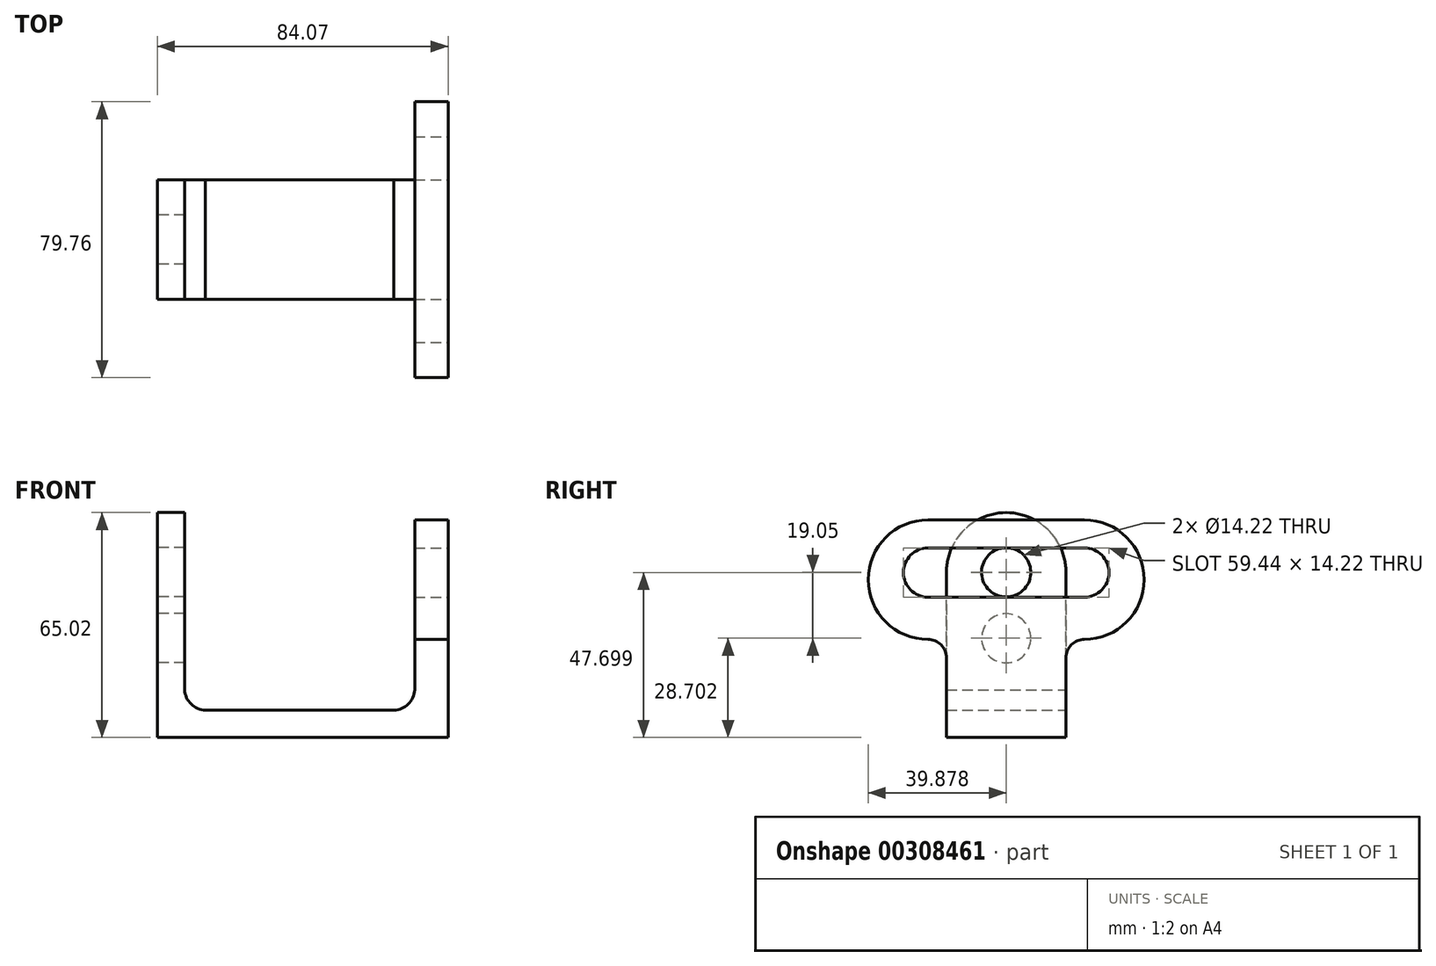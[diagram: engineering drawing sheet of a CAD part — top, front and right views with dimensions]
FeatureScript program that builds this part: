
annotation { "Feature Type Name" : "Feature", "Feature Type Description" : "" }
export const myFeature = defineFeature(function(context is Context, id is Id, definition is map)
    precondition{}
    {
        {
            var Q0;
            Q0=qCreatedBy(makeId("Front.planeOp"),FACE);
            var sketch = newSketch(context, id + "F0", { "sketchPlane" : qUnion([Q0])});
            skLineSegment(sketch, "E0", {"start": v(0, 0) * mm, "end": v(84.07, 0) * mm});
            skLineSegment(sketch, "E1", {"start": v(84.07, 0) * mm, "end": v(84.07, 46.07) * mm});
            skLineSegment(sketch, "E2", {"start": v(84.07, 46.07) * mm, "end": v(74.42, 46.07) * mm});
            skLineSegment(sketch, "E3", {"start": v(74.42, 46.07) * mm, "end": v(74.42, 13.8) * mm});
            skLineSegment(sketch, "E4", {"start": v(68.4, 7.87) * mm, "end": v(13.93, 7.87) * mm});
            skLineSegment(sketch, "E5", {"start": v(7.87, 13.8) * mm, "end": v(7.87, 47.75) * mm});
            skLineSegment(sketch, "E6", {"start": v(7.87, 47.75) * mm, "end": v(0, 47.75) * mm});
            skLineSegment(sketch, "E7", {"start": v(0, 47.75) * mm, "end": v(0, 0) * mm});
            skArc(sketch, "E8", {"start": v(7.87, 13.8) * mm, "mid": v(9.97, 9.49) * mm, "end": v(14.5, 7.87) * mm});
            skArc(sketch, "E9", {"start": v(67.77, 7.87) * mm, "mid": v(72.31, 9.48) * mm, "end": v(74.42, 13.8) * mm});
            skSolve(sketch);
        }
        {
            var Q0;
            Q0 = qSketchRegion(id + "F0", true);
            extrude(context, id + "F1", {"entities" : qUnion([Q0]), "depth" : 34.54 * mm});
        }
        {
            var Q0;
            Q0=makeQuery(id+"F1.opExtrude","SWEPT_FACE",FACE,{"disambiguationData":[OSD([sQuery(id+"F0.wireOp",EDGE,"E7")])]});
            var sketch = newSketch(context, id + "F2", { "sketchPlane" : qUnion([Q0])});
            skArc(sketch, "E10", {"start": v(34.54, 47.75) * mm, "mid": v(17.27, 65.02) * mm, "end": v(0, 47.75) * mm});
            skLineSegment(sketch, "E11", {"start": v(0, 47.75) * mm, "end": v(0, 0) * mm});
            skLineSegment(sketch, "E12", {"start": v(0, 0) * mm, "end": v(34.54, 0) * mm});
            skLineSegment(sketch, "E13", {"start": v(34.54, 0) * mm, "end": v(34.54, 47.75) * mm});
            skCircle(sketch, "E14", {"center": v(17.27, 47.75) * mm, "radius": 7.11 * mm});
            skCircle(sketch, "E15", {"center": v(17.27, 28.7) * mm, "radius": 7.11 * mm});
            skSolve(sketch);
        }
        {
            var Q0;
            Q0 = qSketchRegion(id + "F2", true);
            var Q1;
            Q1=makeQuery(id+"F1.opExtrude","SWEPT_FACE",FACE,{"disambiguationData":[OSD([sQuery(id+"F0.wireOp",EDGE,"E5")])]});
            extrude(context, id + "F3", {"entities" : qUnion([Q0]), "operationType" : NewBodyOperationType.ADD, "endBound" : BoundingType.UP_TO_SURFACE, "oppositeDirection" : true, "endBoundEntityFace" : qUnion([Q1]), "depth" : 25.4 * mm});
        }
        {
            var Q0;
            {var subQ0=sQuery(id+"F2.wireOp",EDGE,"E14");var subQ1=makeQuery(id+"F1.opExtrude","SWEPT_EDGE",EDGE,{"disambiguationData":[OSD([sQuery(id+"F0.wireOp",EDGE,"E6"),sQuery(id+"F0.wireOp",EDGE,"E7")])]});var subQ2=makeQuery(id+"F2.imprint","INTERSECT",VERTEX,{"disambiguationData":[OD(0.0)],"derivedFrom":[subQ1,subQ0]});Q0=makeQuery(id+"F2.imprint","IMPRINT",FACE,{"disambiguationData":[TD([[makeQuery(id+"F2.imprint","IMPRINT",EDGE,{"disambiguationData":[TD([[subQ2,-1.0]])],"derivedFrom":subQ0}),1.0]])]});}
            var Q1;
            Q1=makeQuery(id+"F2.imprint","IMPRINT",FACE,{"disambiguationData":[TD([[makeQuery(id+"F2.imprint","IMPRINT",EDGE,{"derivedFrom":sQuery(id+"F2.wireOp",EDGE,"E15")}),1.0]])]});
            extrude(context, id + "F4", {"entities" : qUnion([Q0, Q1]), "operationType" : NewBodyOperationType.REMOVE, "oppositeDirection" : true, "depth" : 25.4 * mm});
        }
        {
            var Q0;
            Q0=makeQuery(id+"F1.opExtrude","SWEPT_FACE",FACE,{"disambiguationData":[OSD([sQuery(id+"F0.wireOp",EDGE,"E1")])]});
            var sketch = newSketch(context, id + "F5", { "sketchPlane" : qUnion([Q0])});
            skLineSegment(sketch, "E16", {"start": v(-34.54, 0) * mm, "end": v(-34.54, 23.04) * mm});
            skLineSegment(sketch, "E17", {"start": v(0, 23.04) * mm, "end": v(0, 0) * mm});
            skLineSegment(sketch, "E18", {"start": v(0, 0) * mm, "end": v(-34.54, 0) * mm});
            skLineSegment(sketch, "E19", {"start": v(-39.88, 62.91) * mm, "end": v(5.33, 62.91) * mm});
            skLineSegment(sketch, "E20", {"start": v(-39.88, 54.81) * mm, "end": v(5.33, 54.81) * mm});
            skLineSegment(sketch, "E21", {"start": v(-39.88, 40.59) * mm, "end": v(5.33, 40.59) * mm});
            skArc(sketch, "E22", {"start": v(-39.88, 54.81) * mm, "mid": v(-47, 47.7) * mm, "end": v(-39.88, 40.59) * mm});
            skArc(sketch, "E23", {"start": v(5.33, 40.59) * mm, "mid": v(12.45, 47.7) * mm, "end": v(5.33, 54.81) * mm});
            skArc(sketch, "E24", {"start": v(-39.88, 62.91) * mm, "mid": v(-57.15, 45.64) * mm, "end": v(-39.88, 28.37) * mm});
            skArc(sketch, "E25", {"start": v(5.33, 28.37) * mm, "mid": v(22.6, 45.64) * mm, "end": v(5.33, 62.91) * mm});
            skArc(sketch, "E26", {"start": v(-34.54, 23.04) * mm, "mid": v(-36.1, 26.8) * mm, "end": v(-39.88, 28.37) * mm});
            skArc(sketch, "E27", {"start": v(5.33, 28.37) * mm, "mid": v(1.56, 26.8) * mm, "end": v(0, 23.04) * mm});
            skPoint(sketch, "E28.orphan", {"position": v(0, 28.37) * mm});
            skSolve(sketch);
        }
        {
            var Q0;
            Q0 = qSketchRegion(id + "F5", true);
            var Q1;
            Q1=makeQuery(id+"F1.opExtrude","SWEPT_FACE",FACE,{"disambiguationData":[OSD([sQuery(id+"F0.wireOp",EDGE,"E3")])]});
            extrude(context, id + "F6", {"entities" : qUnion([Q0]), "operationType" : NewBodyOperationType.ADD, "endBound" : BoundingType.UP_TO_SURFACE, "oppositeDirection" : true, "endBoundEntityFace" : qUnion([Q1]), "depth" : 25.4 * mm});
        }
        {
            var Q0;
            Q0=makeQuery(id+"F6.boolean.opBoolean","MERGE",FACE,{"derivedFrom":[makeQuery(id+"F1.opExtrude","SWEPT_FACE",FACE,{"disambiguationData":[OSD([sQuery(id+"F0.wireOp",EDGE,"E1")])]}),makeQuery(id+"F6.opExtrude","CAP_FACE",FACE,{"disambiguationData":[OSD([sQuery(id+"F5.wireOp",EDGE,"E16"),sQuery(id+"F5.wireOp",EDGE,"E17"),sQuery(id+"F5.wireOp",EDGE,"E18"),sQuery(id+"F5.wireOp",EDGE,"E19"),sQuery(id+"F5.wireOp",EDGE,"E20"),sQuery(id+"F5.wireOp",EDGE,"E21"),sQuery(id+"F5.wireOp",EDGE,"E22"),sQuery(id+"F5.wireOp",EDGE,"E23"),sQuery(id+"F5.wireOp",EDGE,"E24"),sQuery(id+"F5.wireOp",EDGE,"E25"),sQuery(id+"F5.wireOp",EDGE,"E26"),sQuery(id+"F5.wireOp",EDGE,"E27")])],"isStart":true})]});
            var sketch = newSketch(context, id + "F7", { "sketchPlane" : qUnion([Q0])});
            skLineSegment(sketch, "E29", {"start": v(-34.54, 40.59) * mm, "end": v(0, 40.59) * mm});
            skSolve(sketch);
        }
        {
            var Q0;
            Q0=makeQuery(id+"F7.imprint","IMPRINT",FACE,{"disambiguationData":[TD([[makeQuery(id+"F7.imprint","IMPRINT",EDGE,{"derivedFrom":sQuery(id+"F7.wireOp",EDGE,"E29")}),1.0]])]});
            extrude(context, id + "F8", {"entities" : qUnion([Q0]), "operationType" : NewBodyOperationType.REMOVE, "oppositeDirection" : true, "depth" : 25.4 * mm});
        }
    });
